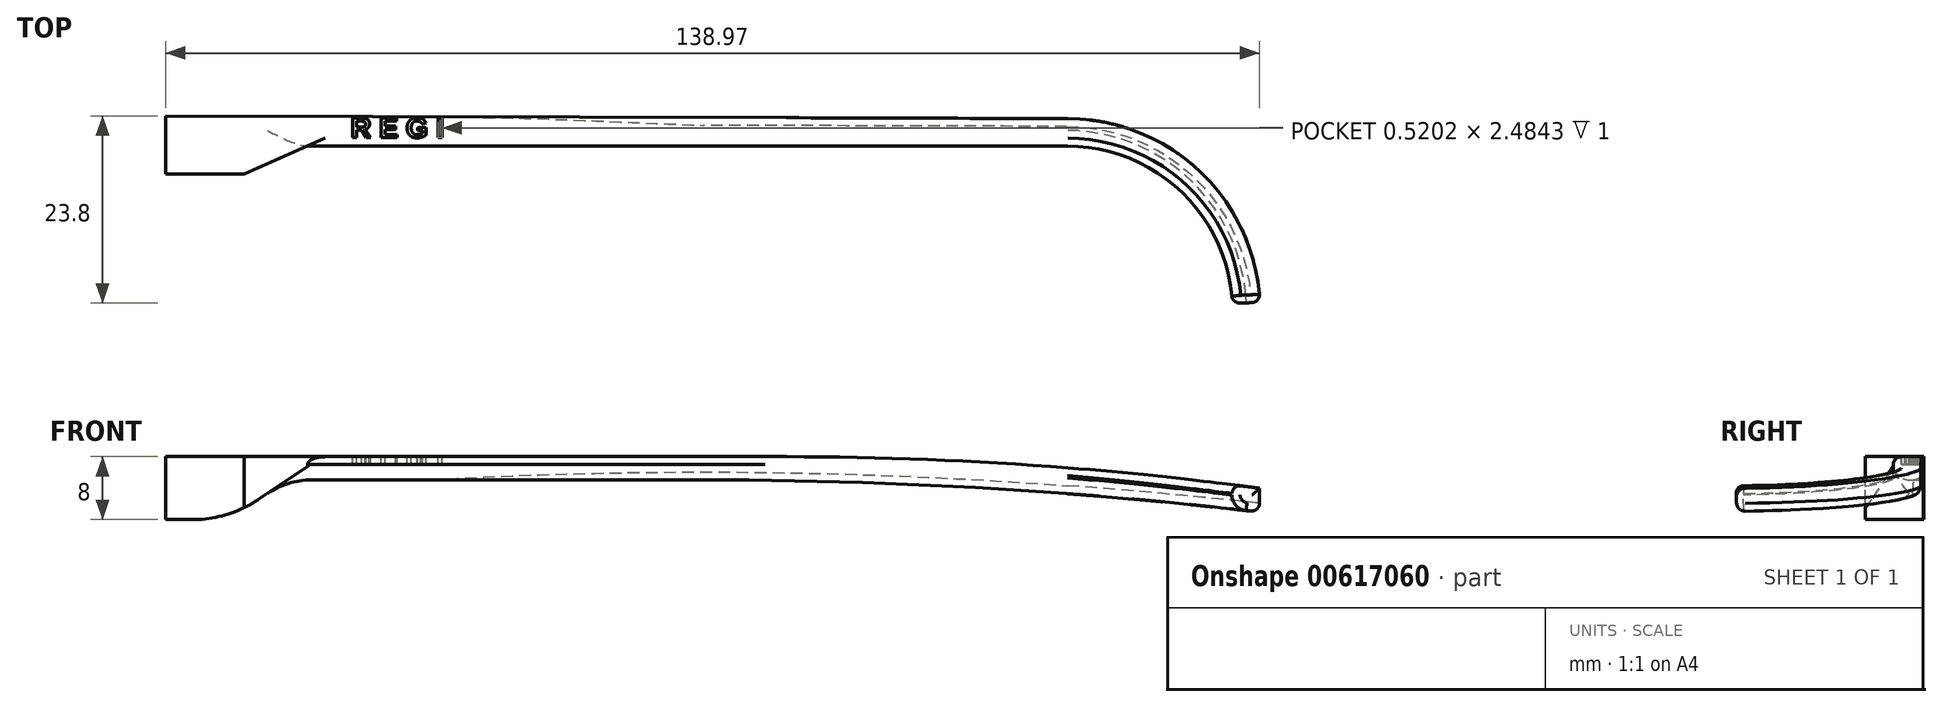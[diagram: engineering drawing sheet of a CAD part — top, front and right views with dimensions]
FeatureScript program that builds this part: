
annotation { "Feature Type Name" : "Feature", "Feature Type Description" : "" }
export const myFeature = defineFeature(function(context is Context, id is Id, definition is map)
    precondition{}
    {
        {
            var Q0;
            Q0=qCreatedBy(makeId("Front.planeOp"),FACE);
            var sketch = newSketch(context, id + "F0", { "sketchPlane" : qUnion([Q0])});
            skLineSegment(sketch, "E0.bottom", {"start": v(0, 0) * mm, "end": v(156.1, 0) * mm});
            skLineSegment(sketch, "E0.top", {"start": v(0, -43.39) * mm, "end": v(156.1, -43.39) * mm});
            skLineSegment(sketch, "E0.left", {"start": v(0, 0) * mm, "end": v(0, -43.39) * mm});
            skLineSegment(sketch, "E0.right", {"start": v(156.1, 0) * mm, "end": v(156.1, -43.39) * mm});
            skSolve(sketch);
        }
        {
            var Q0;
            Q0 = qSketchRegion(id + "F0", true);
            extrude(context, id + "F1", {"entities" : qUnion([Q0]), "depth" : 50 * mm, "offsetDistance" : 25 * mm});
        }
        {
            var Q0;
            Q0=makeQuery(id+"F1.opExtrude","CAP_FACE",FACE,{"disambiguationData":[OSD([sQuery(id+"F0.wireOp",EDGE,"E0.bottom"),sQuery(id+"F0.wireOp",EDGE,"E0.top"),sQuery(id+"F0.wireOp",EDGE,"E0.left"),sQuery(id+"F0.wireOp",EDGE,"E0.right")])],"isStart":true});
            var sketch = newSketch(context, id + "F2", { "sketchPlane" : qUnion([Q0])});
            skLineSegment(sketch, "E1", {"start": v(0, -9.84) * mm, "end": v(-78.92, -9.84) * mm});
            skLineSegment(sketch, "E2", {"start": v(-140, -14) * mm, "end": v(-139.8, -16.98) * mm});
            skLineSegment(sketch, "E3", {"start": v(-68.39, -12.79) * mm, "end": v(-15.5, -12.79) * mm});
            skLineSegment(sketch, "E4", {"start": v(-15.5, -12.79) * mm, "end": v(-8, -17.84) * mm});
            skLineSegment(sketch, "E5", {"start": v(-8, -17.84) * mm, "end": v(0, -17.84) * mm});
            skArc(sketch, "E6", {"start": v(-68.39, -12.79) * mm, "mid": v(-104.15, -13.84) * mm, "end": v(-139.8, -16.98) * mm});
            skArc(sketch, "E7", {"start": v(-78.92, -9.84) * mm, "mid": v(-109.53, -10.88) * mm, "end": v(-140, -14) * mm});
            skLineSegment(sketch, "E8.bottom", {"start": v(-156.1, 0) * mm, "end": v(0, 0) * mm});
            skLineSegment(sketch, "E8.top", {"start": v(-156.1, -43.39) * mm, "end": v(0, -43.39) * mm});
            skLineSegment(sketch, "E8.left", {"start": v(-156.1, 0) * mm, "end": v(-156.1, -43.39) * mm});
            skLineSegment(sketch, "E8.right", {"start": v(0, 0) * mm, "end": v(0, -9.84) * mm});
            skLineSegment(sketch, "E9.trimOffspring", {"start": v(0, -17.84) * mm, "end": v(0, -43.39) * mm});
            skSolve(sketch);
        }
        {
            var Q0;
            Q0 = qSketchRegion(id + "F2", true);
            extrude(context, id + "F3", {"entities" : qUnion([Q0]), "operationType" : NewBodyOperationType.REMOVE, "endBound" : BoundingType.THROUGH_ALL, "oppositeDirection" : true, "depth" : 25 * mm, "offsetDistance" : 25 * mm});
        }
        {
            var Q0;
            Q0=qCreatedBy(makeId("Top.planeOp"),FACE);
            var sketch = newSketch(context, id + "F4", { "sketchPlane" : qUnion([Q0])});
            skLineSegment(sketch, "E10", {"start": v(0, -7.38) * mm, "end": v(10, -7.38) * mm});
            skLineSegment(sketch, "E11", {"start": v(10, -7.38) * mm, "end": v(18.04, -3.85) * mm});
            skLineSegment(sketch, "E12", {"start": v(18.04, -3.85) * mm, "end": v(114.57, -3.85) * mm});
            skArc(sketch, "E13", {"start": v(135.54, -23.84) * mm, "mid": v(129.05, -9.65) * mm, "end": v(114.57, -3.85) * mm});
            skArc(sketch, "E14.0", {"start": v(139.03, -23.68) * mm, "mid": v(131.47, -7.12) * mm, "end": v(114.57, -0.35) * mm});
            skLineSegment(sketch, "E15", {"start": v(135.54, -23.84) * mm, "end": v(139.03, -23.68) * mm});
            skLineSegment(sketch, "E16", {"start": v(114.57, -0.35) * mm, "end": v(0, 0) * mm});
            skLineSegment(sketch, "E17.0", {"start": v(78.92, 0) * mm, "end": v(140, 0) * mm});
            skLineSegment(sketch, "E18.0", {"start": v(0, 0) * mm, "end": v(78.92, 0) * mm});
            skLineSegment(sketch, "E19.0", {"start": v(140, -50) * mm, "end": v(140, 0) * mm});
            skLineSegment(sketch, "E20.0", {"start": v(140, -50) * mm, "end": v(78.92, -50) * mm});
            skLineSegment(sketch, "E21.0", {"start": v(78.92, -50) * mm, "end": v(0, -50) * mm});
            skLineSegment(sketch, "E22.0", {"start": v(0, -50) * mm, "end": v(0, -7.38) * mm});
            skSolve(sketch);
        }
        {
            var Q0;
            Q0 = qSketchRegion(id + "F4", true);
            extrude(context, id + "F5", {"entities" : qUnion([Q0]), "operationType" : NewBodyOperationType.REMOVE, "oppositeDirection" : true, "depth" : 25 * mm, "offsetDistance" : 25 * mm});
        }
        {
            var Q0;
            Q0=makeQuery(id+"F3.boolean.opBoolean","COPY",EDGE,{"derivedFrom":makeQuery(id+"F3.opExtrude","SWEPT_EDGE",EDGE,{"disambiguationData":[OSD([sQuery(id+"F2.wireOp",EDGE,"E4"),sQuery(id+"F2.wireOp",EDGE,"E5")])]})});
            fillet(context, id + "F6", {"entities" : qUnion([Q0]), "radius" : 15 * mm, "tangentPropagation" : true, "allowEdgeOverflow" : false});
        }
        {
            var Q0;
            Q0=makeQuery(id+"F3.boolean.opBoolean","COPY",EDGE,{"derivedFrom":makeQuery(id+"F3.opExtrude","SWEPT_EDGE",EDGE,{"disambiguationData":[OSD([sQuery(id+"F2.wireOp",EDGE,"E3"),sQuery(id+"F2.wireOp",EDGE,"E4")])]})});
            fillet(context, id + "F7", {"entities" : qUnion([Q0]), "radius" : 10 * mm, "tangentPropagation" : true, "allowEdgeOverflow" : false});
        }
        {
            var Q0;
            Q0=makeQuery(id+"F5.boolean.opBoolean","INTERSECT",EDGE,{"derivedFrom":[makeQuery(id+"F3.boolean.opBoolean","COPY",FACE,{"derivedFrom":makeQuery(id+"F3.opExtrude","SWEPT_FACE",FACE,{"disambiguationData":[OSD([sQuery(id+"F2.wireOp",EDGE,"E3")])]})}),makeQuery(id+"F5.opExtrude","SWEPT_FACE",FACE,{"disambiguationData":[OSD([sQuery(id+"F4.wireOp",EDGE,"E12")])]})]});
            fillet(context, id + "F8", {"entities" : qUnion([Q0]), "radius" : 2 * mm, "tangentPropagation" : true, "allowEdgeOverflow" : false});
        }
        {
            var Q0;
            Q0=makeQuery(id+"F5.boolean.opBoolean","INTERSECT",EDGE,{"derivedFrom":[makeQuery(id+"F3.boolean.opBoolean","COPY",FACE,{"derivedFrom":makeQuery(id+"F3.opExtrude","SWEPT_FACE",FACE,{"disambiguationData":[OSD([sQuery(id+"F2.wireOp",EDGE,"E6")])]})}),makeQuery(id+"F5.opExtrude","SWEPT_FACE",FACE,{"disambiguationData":[OSD([sQuery(id+"F4.wireOp",EDGE,"E14.0")])]})]});
            var Q1;
            Q1=makeQuery(id+"F5.boolean.opBoolean","INTERSECT",EDGE,{"derivedFrom":[makeQuery(id+"F3.boolean.opBoolean","COPY",FACE,{"derivedFrom":makeQuery(id+"F3.opExtrude","SWEPT_FACE",FACE,{"disambiguationData":[OSD([sQuery(id+"F2.wireOp",EDGE,"E6")])]})}),makeQuery(id+"F5.opExtrude","SWEPT_FACE",FACE,{"disambiguationData":[OSD([sQuery(id+"F4.wireOp",EDGE,"E15")])]})]});
            var Q2;
            Q2=makeQuery(id+"F5.boolean.opBoolean","COPY",EDGE,{"derivedFrom":makeQuery(id+"F5.opExtrude","SWEPT_EDGE",EDGE,{"disambiguationData":[OSD([sQuery(id+"F4.wireOp",EDGE,"E14.0"),sQuery(id+"F4.wireOp",EDGE,"E15")])]})});
            var Q3;
            Q3=makeQuery(id+"F5.boolean.opBoolean","INTERSECT",EDGE,{"derivedFrom":[makeQuery(id+"F3.boolean.opBoolean","COPY",FACE,{"derivedFrom":makeQuery(id+"F3.opExtrude","SWEPT_FACE",FACE,{"disambiguationData":[OSD([sQuery(id+"F2.wireOp",EDGE,"E7")])]})}),makeQuery(id+"F5.opExtrude","SWEPT_FACE",FACE,{"disambiguationData":[OSD([sQuery(id+"F4.wireOp",EDGE,"E15")])]})]});
            var Q4;
            Q4=makeQuery(id+"F5.boolean.opBoolean","INTERSECT",EDGE,{"derivedFrom":[makeQuery(id+"F3.boolean.opBoolean","COPY",FACE,{"derivedFrom":makeQuery(id+"F3.opExtrude","SWEPT_FACE",FACE,{"disambiguationData":[OSD([sQuery(id+"F2.wireOp",EDGE,"E7")])]})}),makeQuery(id+"F5.opExtrude","SWEPT_FACE",FACE,{"disambiguationData":[OSD([sQuery(id+"F4.wireOp",EDGE,"E13")])]})]});
            fillet(context, id + "F9", {"entities" : qUnion([Q0, Q1, Q2, Q3, Q4]), "radius" : 1 * mm, "tangentPropagation" : true, "allowEdgeOverflow" : false});
        }
        {
            var Q0;
            Q0=makeQuery(id+"F3.boolean.opBoolean","COPY",FACE,{"derivedFrom":makeQuery(id+"F3.opExtrude","SWEPT_FACE",FACE,{"disambiguationData":[OSD([sQuery(id+"F2.wireOp",EDGE,"E1")])]})});
            var sketch = newSketch(context, id + "F10", { "sketchPlane" : qUnion([Q0])});
            skText(sketch, "E23", { "text": "R E G I", "fontName": "Arimo-Bold.ttf"});
            const initialGuessF10  = {"E23": [0.02353, -0.00277, 1, 0, 0.0026]};
            skSetInitialGuess(sketch, initialGuessF10);
            skSolve(sketch);
        }
        {
            var Q0;
            Q0 = qSketchRegion(id + "F10", true);
            extrude(context, id + "F11", {"entities" : qUnion([Q0]), "operationType" : NewBodyOperationType.REMOVE, "oppositeDirection" : true, "depth" : 1 * mm, "offsetDistance" : 25 * mm});
        }
    });
